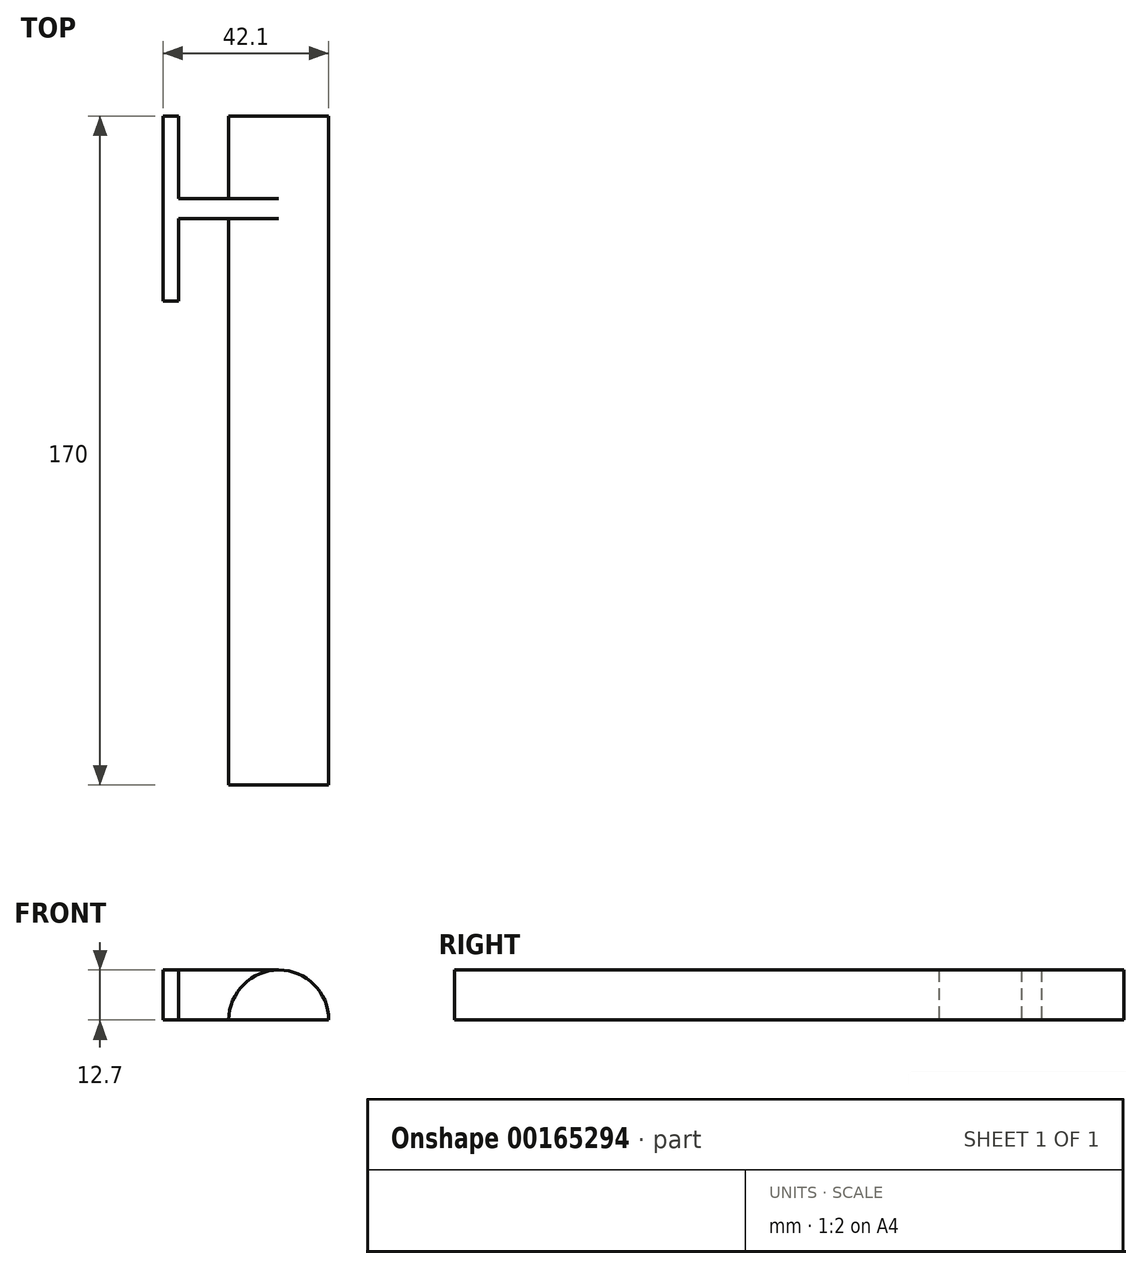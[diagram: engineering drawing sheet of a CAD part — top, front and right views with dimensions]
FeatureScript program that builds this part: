
annotation { "Feature Type Name" : "Feature", "Feature Type Description" : "" }
export const myFeature = defineFeature(function(context is Context, id is Id, definition is map)
    precondition{}
    {
        {
            var Q0;
            Q0=qCreatedBy(makeId("Front.planeOp"),FACE);
            var sketch = newSketch(context, id + "F0", { "sketchPlane" : qUnion([Q0]), "disableImprinting" : false});
            skCircle(sketch, "E0", {"center": v(0, 0) * mm, "radius": 12.7 * mm});
            skCircle(sketch, "E1", {"center": v(0, 0) * mm, "radius": 15.7 * mm});
            skLineSegment(sketch, "E2", {"start": v(-15.7, 0) * mm, "end": v(15.7, 0) * mm});
            skSolve(sketch);
        }
        {
            var Q0;
            {var subQ0=sQuery(id+"F0.wireOp",EDGE,"E2");var subQ1=sQuery(id+"F0.wireOp",EDGE,"E0");var subQ2=makeQuery(id+"F0.imprint","INTERSECT",VERTEX,{"disambiguationData":[OD(0.0)],"derivedFrom":[subQ1,subQ0]});Q0=makeQuery(id+"F0.imprint","IMPRINT",FACE,{"disambiguationData":[TD([[makeQuery(id+"F0.imprint","IMPRINT",EDGE,{"disambiguationData":[TD([[subQ2,1.0]])],"derivedFrom":subQ1}),1.0]])]});}
            extrude(context, id + "F1", {"entities" : qUnion([Q0]), "depth" : 170 * mm});
        }
        {
            var Q0;
            {var subQ0=sQuery(id+"F0.wireOp",EDGE,"E2");Q0=makeQuery(id+"Fhz5QzSXj3IZ3Rl_1.boolean.opBoolean","MERGE",FACE,{"derivedFrom":[makeQuery(id+"Fz5IylH0BVaj6Gj_1.boolean.opBoolean","MERGE",FACE,{"derivedFrom":[makeQuery(id+"F1.opExtrude","SWEPT_FACE",FACE,{"disambiguationData":[OSD([subQ0])]}),makeQuery(id+"Fz5IylH0BVaj6Gj_1.opExtrude","SWEPT_FACE",FACE,{"disambiguationData":[OSD([subQ0])]})]}),makeQuery(id+"Fhz5QzSXj3IZ3Rl_1.opExtrude","SWEPT_FACE",FACE,{"disambiguationData":[OSD([sQuery(id+"FTPX5xXCBAGYZSD_1.wireOp",EDGE,"v9fs1Iau-H1cs-8dii-VVJn-lPa7ASg340Hl")])]})]});}
            var sketch = newSketch(context, id + "F2", { "sketchPlane" : qUnion([Q0])});
            skLineSegment(sketch, "E3.bottom", {"start": v(0, 20.96) * mm, "end": v(-25.4, 20.96) * mm});
            skLineSegment(sketch, "E3.top", {"start": v(0, 26.04) * mm, "end": v(-25.4, 26.04) * mm});
            skLineSegment(sketch, "E3.left", {"start": v(0, 20.96) * mm, "end": v(0, 26.04) * mm});
            skLineSegment(sketch, "E3.right", {"start": v(-25.4, 20.96) * mm, "end": v(-25.4, 26.04) * mm});
            skSolve(sketch);
        }
        {
            var Q0;
            {var subQ0=sQuery(id+"F2.wireOp",EDGE,"E3.left");Q0=makeQuery(id+"F2.imprint","IMPRINT",FACE,{"disambiguationData":[TD([[makeQuery(id+"F2.imprint","IMPRINT",EDGE,{"derivedFrom":subQ0}),1.0]])]});}
            var Q1;
            {var subQ0=sQuery(id+"F2.wireOp",EDGE,"E3.right");Q1=makeQuery(id+"F2.imprint","IMPRINT",FACE,{"disambiguationData":[TD([[makeQuery(id+"F2.imprint","IMPRINT",EDGE,{"derivedFrom":subQ0}),-1.0]])]});}
            var Q2;
            Q2=makeQuery(id+"F1.opExtrude","SWEPT_FACE",FACE,{"disambiguationData":[OSD([sQuery(id+"F0.wireOp",EDGE,"E0")])]});
            var Q3;
            Q3=makeQuery(id+"F1.opExtrude","SWEPT_BODY",BODY,{"disambiguationData":[OSD([sQuery(id+"F0.wireOp",EDGE,"E0"),sQuery(id+"F0.wireOp",EDGE,"E2")])]});
            extrude(context, id + "F3", {"entities" : qUnion([Q0, Q1]), "operationType" : NewBodyOperationType.ADD, "oppositeDirection" : true, "endBoundEntityFace" : qUnion([Q2]), "endBoundEntityBody" : qUnion([Q3]), "depth" : 12.7 * mm});
        }
        {
            var Q0;
            Q0=makeQuery(id+"F3.opExtrude","SWEPT_FACE",FACE,{"disambiguationData":[OSD([sQuery(id+"F2.wireOp",EDGE,"E3.right")])]});
            var sketch = newSketch(context, id + "F4", { "sketchPlane" : qUnion([Q0])});
            skLineSegment(sketch, "E4.bottom", {"start": v(23.5, 12.7) * mm, "end": v(0, 12.7) * mm});
            skLineSegment(sketch, "E4.top", {"start": v(23.5, 0) * mm, "end": v(0, 0) * mm});
            skLineSegment(sketch, "E4.left", {"start": v(23.5, 12.7) * mm, "end": v(23.5, 0) * mm});
            skLineSegment(sketch, "E4.right", {"start": v(0, 12.7) * mm, "end": v(0, 0) * mm});
            skLineSegment(sketch, "E5.bottom", {"start": v(23.5, 12.7) * mm, "end": v(47, 12.7) * mm});
            skLineSegment(sketch, "E5.top", {"start": v(23.5, 0) * mm, "end": v(47, 0) * mm});
            skLineSegment(sketch, "E5.right", {"start": v(47, 12.7) * mm, "end": v(47, 0) * mm});
            skSolve(sketch);
        }
        {
            var Q0;
            {var subQ2=sQuery(id+"F4.wireOp",EDGE,"E5.right");Q0=makeQuery(id+"F4.imprint","IMPRINT",FACE,{"disambiguationData":[TD([[makeQuery(id+"F4.imprint","IMPRINT",EDGE,{"derivedFrom":subQ2}),-1.0]])]});}
            var Q1;
            {var subQ2=sQuery(id+"F4.wireOp",EDGE,"E4.right");Q1=makeQuery(id+"F4.imprint","IMPRINT",FACE,{"disambiguationData":[TD([[makeQuery(id+"F4.imprint","IMPRINT",EDGE,{"derivedFrom":subQ2}),1.0]])]});}
            var Q2;
            {var subQ2=sQuery(id+"F4.wireOp",EDGE,"E4.left");Q2=makeQuery(id+"F4.imprint","IMPRINT",FACE,{"disambiguationData":[TD([[makeQuery(id+"F4.imprint","IMPRINT",EDGE,{"derivedFrom":subQ2}),-1.0]])]});}
            var Q3;
            {var subQ2=sQuery(id+"F4.wireOp",EDGE,"E4.left");Q3=makeQuery(id+"F4.imprint","IMPRINT",FACE,{"disambiguationData":[TD([[makeQuery(id+"F4.imprint","IMPRINT",EDGE,{"derivedFrom":subQ2}),1.0]])]});}
            extrude(context, id + "F5", {"entities" : qUnion([Q0, Q1, Q2, Q3]), "operationType" : NewBodyOperationType.ADD, "depth" : 4 * mm});
        }
    });
